# Revit family: K10.2 - Freespace
name_source: partatom
category: Communication Devices
revit_build: Autodesk Revit 2017 (Build: 20190508_0315(x64)
units: mm (PartAtom-declared; Revit-internal decimal feet)

## family parameters
Always vertical = No
Cut with Voids When Loaded = No
Maintain Annotation Orientation = No
Part Type = Normal
Room Calculation Point = No
Round Connector Dimension = Use Diameter
Shared = No
Work Plane-Based = Yes

## types (1)
- K10.2 - Freespace
    Coverage Horizontal = 90.00°
    Coverage Vertical = 90.00°
    Default Elevation = 0 mm  [stored 0 ft]
    Depth = 300 mm
    Description = Multi-purpose, 2-way active loudspeaker
    Height = 519 mm
    Manufacturer = QSC
    Manufacturer URL = qsc.com
    Model = K10.2
    Product Documentation Link = https://www.qsc.com
    Product Page URL = https://www.qsc.com
    Regulatory Compliance = CE, RAEE, UL, China RoHS, RoHS II, FCC Class B
    SPL Max = 130
    Weight Dimensional (kg) = 17.6
    Weight Dimensional (lb) = 38.8
    Weight Product (kg) = 14.5
    Weight Product (lb) = 32
    Width = 320 mm  [stored 1.04987 ft]

note: [stored X ft] marks values corroborated as IEEE doubles in the binary element streams (Revit-internal decimal feet)

## geometry (parser evidence)
native form markers: Sweep x10
no freeform markers — native parametric forms only
